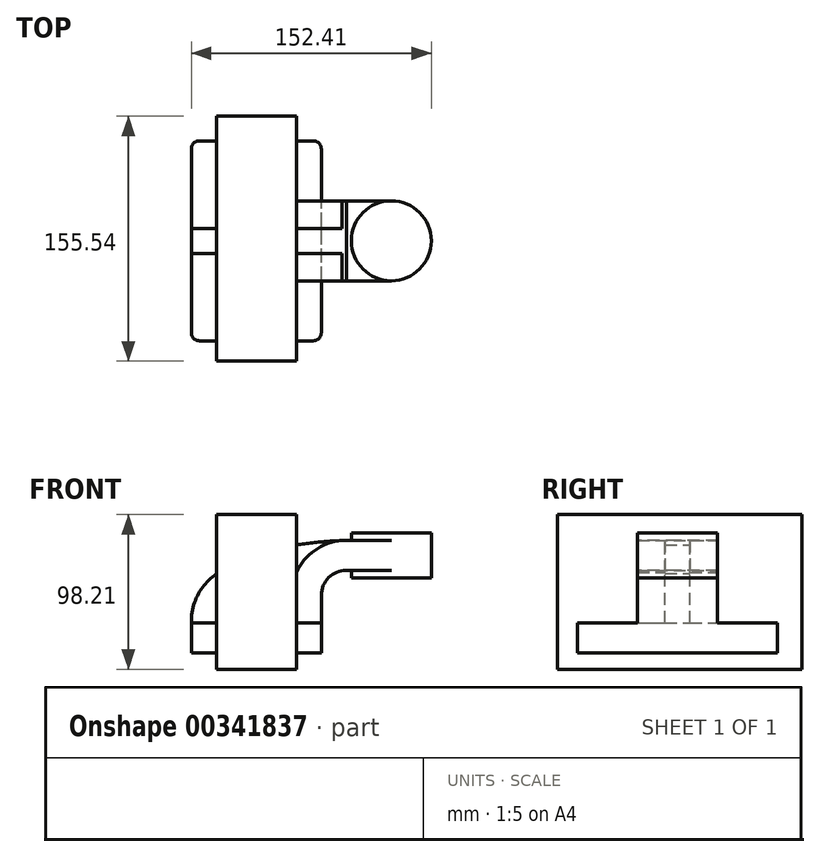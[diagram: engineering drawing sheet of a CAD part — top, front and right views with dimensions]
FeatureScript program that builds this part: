
annotation { "Feature Type Name" : "Feature", "Feature Type Description" : "" }
export const myFeature = defineFeature(function(context is Context, id is Id, definition is map)
    precondition{}
    {
        {
            var Q0;
            Q0=qCreatedBy(makeId("Front.planeOp"),FACE);
            var sketch = newSketch(context, id + "F0", { "sketchPlane" : qUnion([Q0])});
            skLineSegment(sketch, "E0.rect.bottom", {"start": v(-41.28, 9.52) * mm, "end": v(41.28, 9.52) * mm});
            skLineSegment(sketch, "E0.rect.top", {"start": v(-41.28, -9.52) * mm, "end": v(41.28, -9.52) * mm});
            skLineSegment(sketch, "E0.rect.left", {"start": v(-41.28, 9.52) * mm, "end": v(-41.28, -9.52) * mm});
            skLineSegment(sketch, "E0.rect.right", {"start": v(41.28, 9.52) * mm, "end": v(41.28, -9.52) * mm});
            skPoint(sketch, "E0.rect.middle", {"position": v(0, 0) * mm});
            skLineSegment(sketch, "E1", {"start": v(41.28, 9.52) * mm, "end": v(41.28, 27) * mm});
            skArc(sketch, "E2", {"start": v(41.28, 27) * mm, "mid": v(45.92, 38.23) * mm, "end": v(57.15, 42.88) * mm});
            skLineSegment(sketch, "E3", {"start": v(57.15, 42.88) * mm, "end": v(85.72, 42.88) * mm});
            skLineSegment(sketch, "E4.rect.bottom", {"start": v(60.32, 38.1) * mm, "end": v(111.12, 38.1) * mm});
            skLineSegment(sketch, "E4.rect.top", {"start": v(60.32, 66.68) * mm, "end": v(111.12, 66.68) * mm});
            skLineSegment(sketch, "E4.rect.left", {"start": v(60.32, 38.1) * mm, "end": v(60.32, 66.68) * mm});
            skLineSegment(sketch, "E4.rect.right", {"start": v(111.13, 38.1) * mm, "end": v(111.12, 66.68) * mm});
            skPoint(sketch, "E4.rect.middle", {"position": v(85.72, 52.39) * mm});
            skLineSegment(sketch, "E5.0", {"start": v(57.15, 61.93) * mm, "end": v(85.72, 61.93) * mm});
            skArc(sketch, "E5.1", {"start": v(22.23, 27) * mm, "mid": v(32.45, 51.7) * mm, "end": v(57.15, 61.93) * mm});
            skLineSegment(sketch, "E5.2", {"start": v(22.23, 9.52) * mm, "end": v(22.23, 27) * mm});
            skLineSegment(sketch, "E6", {"start": v(85.72, 38.1) * mm, "end": v(85.72, 66.68) * mm});
            skFitSpline(sketch, "E7", {"points": [v(-41.28, 9.53) * mm, v(57.15, 61.93) * mm], "startDerivative": vector(-1.72, 123.73) * mm, "endDerivative": vector(120.92, 4.22) * mm});
            skSolve(sketch);
        }
        {
            var Q0;
            Q0=makeQuery(id+"F0.imprint","IMPRINT",FACE,{"disambiguationData":[TD([[makeQuery(id+"F0.imprint","IMPRINT",EDGE,{"derivedFrom":sQuery(id+"F0.wireOp",EDGE,"E0.rect.top")}),1.0]])]});
            extrude(context, id + "F1", {"entities" : qUnion([Q0]), "endBound" : BoundingType.SYMMETRIC, "depth" : 127 * mm});
        }
        {
            var Q0;
            {var subQ9=sQuery(id+"F0.wireOp",EDGE,"E1");Q0=makeQuery(id+"F0.imprint","IMPRINT",FACE,{"disambiguationData":[TD([[makeQuery(id+"F0.imprint","IMPRINT",EDGE,{"derivedFrom":subQ9}),1.0]])]});}
            var Q1;
            {var subQ0=sQuery(id+"F0.wireOp",EDGE,"E6");var subQ1=sQuery(id+"F0.wireOp",EDGE,"E3");var subQ2=makeQuery(id+"F0.imprint","INTERSECT",VERTEX,{"derivedFrom":[subQ1,subQ0]});Q1=makeQuery(id+"F0.imprint","IMPRINT",FACE,{"disambiguationData":[TD([[makeQuery(id+"F0.imprint","IMPRINT",EDGE,{"disambiguationData":[TD([[subQ2,1.0]])],"derivedFrom":subQ1}),1.0]])]});}
            extrude(context, id + "F2", {"entities" : qUnion([Q0, Q1]), "operationType" : NewBodyOperationType.ADD, "endBound" : BoundingType.SYMMETRIC, "depth" : 50.8 * mm});
        }
        {
            var Q0;
            {var subQ3=sQuery(id+"F0.wireOp",EDGE,"E5.2");Q0=makeQuery(id+"F0.imprint","IMPRINT",FACE,{"disambiguationData":[TD([[makeQuery(id+"F0.imprint","IMPRINT",EDGE,{"derivedFrom":subQ3}),1.0]])]});}
            extrude(context, id + "F3", {"entities" : qUnion([Q0]), "operationType" : NewBodyOperationType.ADD, "endBound" : BoundingType.SYMMETRIC, "depth" : 15.88 * mm});
        }
        {
            var Q0;
            {var subQ5=sQuery(id+"F0.wireOp",EDGE,"E4.rect.right");Q0=makeQuery(id+"F0.imprint","IMPRINT",FACE,{"disambiguationData":[TD([[makeQuery(id+"F0.imprint","IMPRINT",EDGE,{"derivedFrom":subQ5}),1.0]])]});}
            var Q1;
            Q1=sQuery(id+"F0.wireOp",EDGE,"E6");
            revolve(context, id + "F4", {"operationType" : NewBodyOperationType.ADD, "entities" : qUnion([Q0]), "axis" : qUnion([Q1]), "revolveType" : RevolveType.FULL});
        }
        {
            var Q0;
            Q0=makeQuery(id+"F1.opExtrude","CAP_EDGE",EDGE,{"disambiguationData":[OSD([sQuery(id+"F0.wireOp",EDGE,"E0.rect.right")])],"isStart":false});
            var Q1;
            Q1=makeQuery(id+"F1.opExtrude","CAP_EDGE",EDGE,{"disambiguationData":[OSD([sQuery(id+"F0.wireOp",EDGE,"E0.rect.left")])],"isStart":false});
            var Q2;
            Q2=makeQuery(id+"F1.opExtrude","CAP_EDGE",EDGE,{"disambiguationData":[OSD([sQuery(id+"F0.wireOp",EDGE,"E0.rect.right")])],"isStart":true});
            var Q3;
            Q3=makeQuery(id+"F1.opExtrude","CAP_EDGE",EDGE,{"disambiguationData":[OSD([sQuery(id+"F0.wireOp",EDGE,"E0.rect.left")])],"isStart":true});
            fillet(context, id + "F5", {"entities" : qUnion([Q0, Q1, Q2, Q3]), "radius" : 5.08 * mm, "tangentPropagation" : true, "allowEdgeOverflow" : false});
        }
        {
            var Q0;
            Q0=qCreatedBy(makeId("Right.planeOp"),FACE);
            var sketch = newSketch(context, id + "F6", { "sketchPlane" : qUnion([Q0])});
            skLineSegment(sketch, "E8.bottom", {"start": v(-76.42, 78.27) * mm, "end": v(79.12, 78.27) * mm});
            skLineSegment(sketch, "E8.top", {"start": v(-76.42, -19.94) * mm, "end": v(79.12, -19.94) * mm});
            skLineSegment(sketch, "E8.left", {"start": v(-76.42, 78.27) * mm, "end": v(-76.42, -19.94) * mm});
            skLineSegment(sketch, "E8.right", {"start": v(79.12, 78.27) * mm, "end": v(79.12, -19.94) * mm});
            skSolve(sketch);
        }
        {
            var Q0;
            Q0 = qSketchRegion(id + "F6", true);
            extrude(context, id + "F7", {"entities" : qUnion([Q0]), "operationType" : NewBodyOperationType.ADD, "endBound" : BoundingType.SYMMETRIC, "depth" : 50.8 * mm});
        }
    });
